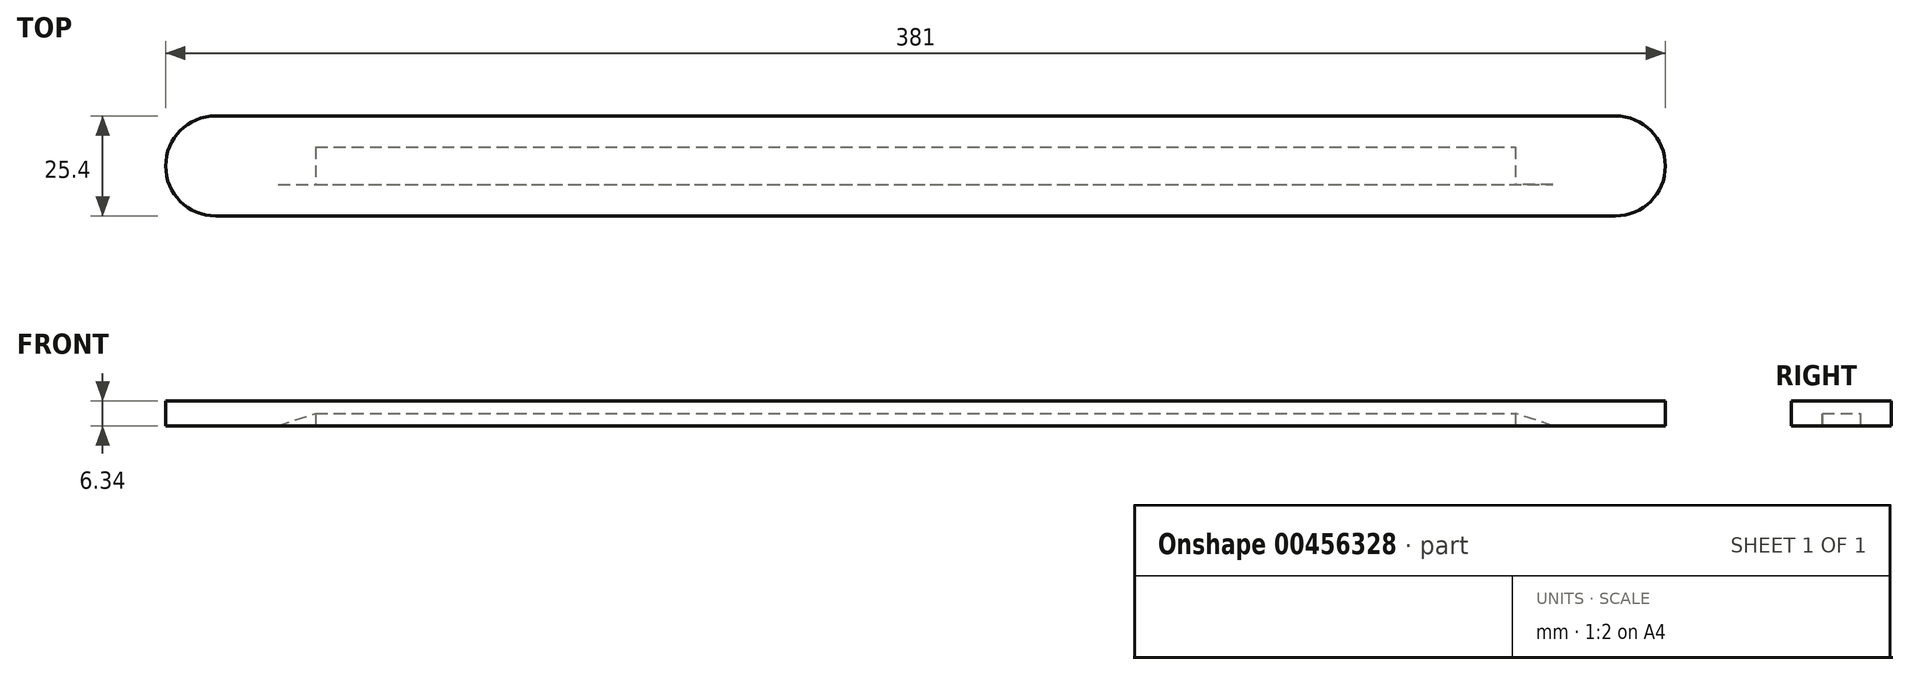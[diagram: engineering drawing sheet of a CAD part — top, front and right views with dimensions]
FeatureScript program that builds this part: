
annotation { "Feature Type Name" : "Feature", "Feature Type Description" : "" }
export const myFeature = defineFeature(function(context is Context, id is Id, definition is map)
    precondition{}
    {
        {
            var Q0;
            Q0=qCreatedBy(makeId("Top.planeOp"),FACE);
            var sketch = newSketch(context, id + "F0", { "sketchPlane" : qUnion([Q0])});
            skPoint(sketch, "E0", {"position": v(-152.4, 12.7) * mm});
            skPoint(sketch, "E1", {"position": v(-152.4, -12.7) * mm});
            skPoint(sketch, "E2", {"position": v(0, 0) * mm});
            skPoint(sketch, "E3", {"position": v(-190.5, 12.7) * mm});
            skPoint(sketch, "E4", {"position": v(-190.5, -12.7) * mm});
            skLineSegment(sketch, "E5", {"start": v(-190.5, 0) * mm, "end": v(190.5, 0) * mm, "construction": true});
            skLineSegment(sketch, "E6", {"start": v(-177.8, 12.7) * mm, "end": v(-152.4, 12.7) * mm});
            skLineSegment(sketch, "E7", {"start": v(-177.8, -12.7) * mm, "end": v(-152.4, -12.7) * mm});
            skLineSegment(sketch, "E8", {"start": v(-190.5, 0) * mm, "end": v(-190.5, 0) * mm});
            skLineSegment(sketch, "E9", {"start": v(0, 12.7) * mm, "end": v(0, -12.7) * mm, "construction": true});
            skPoint(sketch, "E10", {"position": v(-166.37, 0) * mm});
            skArc(sketch, "E11.filletArc", {"start": v(-190.5, 0) * mm, "mid": v(-186.78, -8.98) * mm, "end": v(-177.8, -12.7) * mm});
            skArc(sketch, "E12.filletArc", {"start": v(-177.8, 12.7) * mm, "mid": v(-186.78, 8.98) * mm, "end": v(-190.5, 0) * mm});
            skPoint(sketch, "E13.MirrorP", {"position": v(190.5, -12.7) * mm});
            skPoint(sketch, "E14.MirrorP", {"position": v(190.5, 12.7) * mm});
            skPoint(sketch, "E15.MirrorP", {"position": v(166.37, 0) * mm});
            skPoint(sketch, "E16.MirrorP", {"position": v(152.4, 12.7) * mm});
            skPoint(sketch, "E17.MirrorP", {"position": v(152.4, -12.7) * mm});
            skLineSegment(sketch, "E18.MirrorCS", {"start": v(190.5, 0) * mm, "end": v(-190.5, 0) * mm, "construction": true});
            skLineSegment(sketch, "E19.MirrorCS", {"start": v(177.8, 12.7) * mm, "end": v(152.4, 12.7) * mm});
            skLineSegment(sketch, "E20.MirrorCS", {"start": v(177.8, -12.7) * mm, "end": v(152.4, -12.7) * mm});
            skArc(sketch, "E21.MirrorCS", {"start": v(190.5, 0) * mm, "mid": v(186.78, -8.98) * mm, "end": v(177.8, -12.7) * mm});
            skArc(sketch, "E22.MirrorCS", {"start": v(177.8, 12.7) * mm, "mid": v(186.78, 8.98) * mm, "end": v(190.5, 0) * mm});
            skLineSegment(sketch, "E23.MirrorCS", {"start": v(190.5, 0) * mm, "end": v(190.5, 0) * mm});
            skLineSegment(sketch, "E24", {"start": v(-152.4, 12.7) * mm, "end": v(152.4, 12.7) * mm});
            skLineSegment(sketch, "E25", {"start": v(152.4, -12.7) * mm, "end": v(-152.4, -12.7) * mm});
            skSolve(sketch);
        }
        {
            var Q0;
            Q0=makeQuery(id+"F0.imprint","IMPRINT",FACE,{"disambiguationData":[TD([[makeQuery(id+"F0.imprint","IMPRINT",EDGE,{"derivedFrom":sQuery(id+"F0.wireOp",EDGE,"33ddd2f7-314b-40ee-8d08-8bc8de4d81912.MirrorCS")}),1.0]])]});
            var Q1;
            Q1=makeQuery(id+"F0.imprint","IMPRINT",FACE,{"disambiguationData":[TD([[makeQuery(id+"F0.imprint","IMPRINT",EDGE,{"derivedFrom":sQuery(id+"F0.wireOp",EDGE,"E6")}),-1.0]])]});
            extrude(context, id + "F1", {"entities" : qUnion([Q0, Q1]), "endBound" : BoundingType.SYMMETRIC, "depth" : 6.35 * mm});
        }
        {
            var Q0;
            Q0=qCreatedBy(makeId("Right.planeOp"),FACE);
            var sketch = newSketch(context, id + "F2", { "sketchPlane" : qUnion([Q0])});
            skPoint(sketch, "E26", {"position": v(4.76, 0) * mm});
            skPoint(sketch, "E27", {"position": v(4.76, -3.18) * mm});
            skPoint(sketch, "E28.MirrorP", {"position": v(-4.76, 0) * mm});
            skPoint(sketch, "E29.MirrorP", {"position": v(-4.76, -3.18) * mm});
            skLineSegment(sketch, "E30", {"start": v(4.76, 0) * mm, "end": v(4.76, -3.18) * mm});
            skLineSegment(sketch, "E31", {"start": v(4.76, -3.18) * mm, "end": v(-4.76, -3.18) * mm});
            skLineSegment(sketch, "E32", {"start": v(-4.76, -3.18) * mm, "end": v(-4.76, 0) * mm});
            skLineSegment(sketch, "E33", {"start": v(-4.76, 0) * mm, "end": v(4.76, 0) * mm});
            skSolve(sketch);
        }
        {
            var Q0;
            Q0=makeQuery(id+"F2.imprint","IMPRINT",FACE,{"disambiguationData":[TD([[makeQuery(id+"F2.imprint","IMPRINT",EDGE,{"derivedFrom":sQuery(id+"F2.wireOp",EDGE,"E30")}),-1.0]])]});
            var Q1;
            Q1=makeQuery(id+"F1.opExtrude","SWEPT_FACE",FACE,{"disambiguationData":[OSD([sQuery(id+"F0.wireOp",EDGE,"E11.filletArc"),sQuery(id+"F0.wireOp",EDGE,"E12.filletArc")])]});
            extrude(context, id + "F3", {"entities" : qUnion([Q0]), "operationType" : NewBodyOperationType.REMOVE, "endBound" : BoundingType.SYMMETRIC, "oppositeDirection" : true, "endBoundEntityFace" : qUnion([Q1]), "depth" : 304.8 * mm, "hasSecondDirection" : true, "secondDirectionBound" : SecondDirectionBoundingType.UP_TO_SURFACE, "secondDirectionOppositeDirection" : false, "secondDirectionDepth" : 25.4 * mm});
        }
        {
            var Q0;
            Q0=makeQuery(id+"F3.boolean.opBoolean","COPY",FACE,{"derivedFrom":makeQuery(id+"F3.opExtrude","SWEPT_FACE",FACE,{"disambiguationData":[OSD([sQuery(id+"F2.wireOp",EDGE,"E32")])]})});
            var sketch = newSketch(context, id + "F4", { "sketchPlane" : qUnion([Q0])});
            skPoint(sketch, "E34", {"position": v(152.4, 0) * mm});
            skPoint(sketch, "E35", {"position": v(152.4, -3.18) * mm});
            skLineSegment(sketch, "E36", {"start": v(152.4, 0) * mm, "end": v(152.4, -3.18) * mm});
            skPoint(sketch, "E37", {"position": v(161.93, -3.17) * mm});
            skLineSegment(sketch, "E38", {"start": v(161.93, -3.17) * mm, "end": v(152.4, 0) * mm});
            skLineSegment(sketch, "E39", {"start": v(161.93, -3.18) * mm, "end": v(152.4, -3.18) * mm});
            skLineSegment(sketch, "E40.MirrorCS", {"start": v(-152.4, 0) * mm, "end": v(-152.4, -3.18) * mm});
            skPoint(sketch, "E41.MirrorP", {"position": v(-152.4, 0) * mm});
            skPoint(sketch, "E42.MirrorP", {"position": v(-161.93, -3.17) * mm});
            skLineSegment(sketch, "E43.MirrorCS", {"start": v(-161.93, -3.18) * mm, "end": v(-152.4, -3.18) * mm});
            skLineSegment(sketch, "E44.MirrorCS", {"start": v(-161.93, -3.17) * mm, "end": v(-152.4, 0) * mm});
            skPoint(sketch, "E45.MirrorP", {"position": v(-152.4, -3.18) * mm});
            skSolve(sketch);
        }
        {
            var Q0;
            Q0=makeQuery(id+"F4.imprint","IMPRINT",FACE,{"disambiguationData":[TD([[makeQuery(id+"F4.imprint","IMPRINT",EDGE,{"derivedFrom":sQuery(id+"F4.wireOp",EDGE,"E36")}),-1.0]])]});
            var Q1;
            Q1=makeQuery(id+"F4.imprint","IMPRINT",FACE,{"disambiguationData":[TD([[makeQuery(id+"F4.imprint","IMPRINT",EDGE,{"derivedFrom":sQuery(id+"F4.wireOp",EDGE,"E40.MirrorCS")}),1.0]])]});
            extrude(context, id + "F5", {"entities" : qUnion([Q0, Q1]), "operationType" : NewBodyOperationType.REMOVE, "depth" : 3 / 203.2 * mm});
        }
    });
